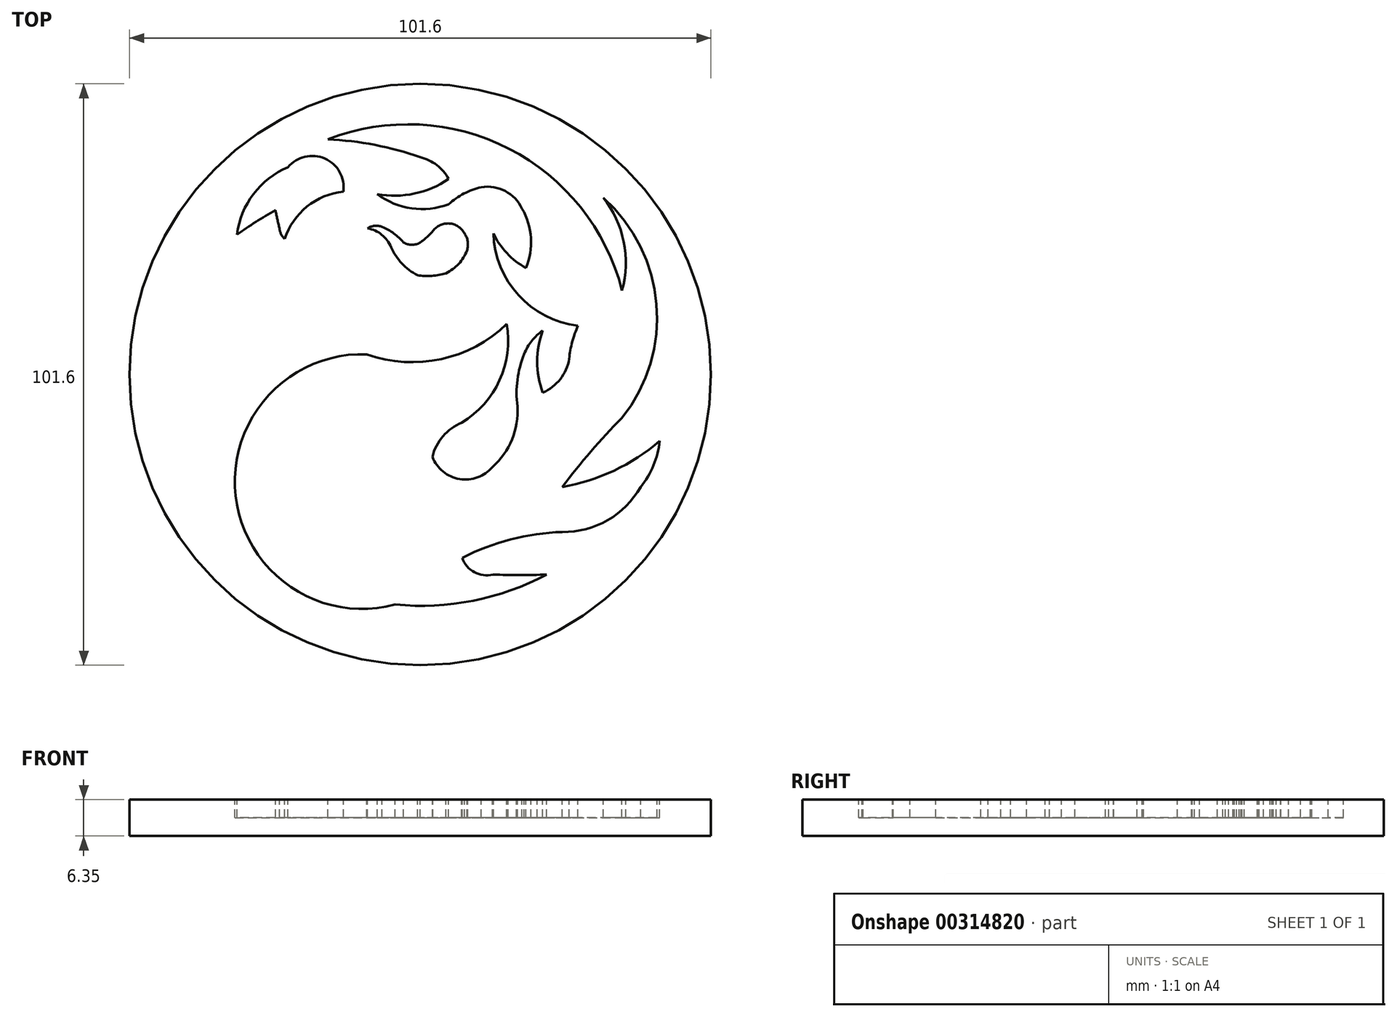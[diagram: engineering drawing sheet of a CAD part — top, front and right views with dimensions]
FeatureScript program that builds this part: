
annotation { "Feature Type Name" : "Feature", "Feature Type Description" : "" }
export const myFeature = defineFeature(function(context is Context, id is Id, definition is map)
    precondition{}
    {
        {
            var Q0;
            Q0=qCreatedBy(makeId("Top.planeOp"),FACE);
            var sketch = newSketch(context, id + "F0", { "sketchPlane" : qUnion([Q0])});
            skCircle(sketch, "E0", {"center": v(0, 0) * mm, "radius": 50.8 * mm});
            skSolve(sketch);
        }
        {
            var Q0;
            Q0 = qSketchRegion(id + "F0", true);
            extrude(context, id + "F1", {"entities" : qUnion([Q0]), "depth" : 6.35 * mm});
        }
        {
            var Q0;
            Q0=makeQuery(id+"F1.opExtrude","CAP_FACE",FACE,{"disambiguationData":[OSD([sQuery(id+"F0.wireOp",EDGE,"E0")])],"isStart":false});
            var sketch = newSketch(context, id + "F2", { "sketchPlane" : qUnion([Q0])});
            skArc(sketch, "E1", {"start": v(-9.32, 3.53) * mm, "mid": v(-32.25, -21.21) * mm, "end": v(-4.37, -40.2) * mm});
            skArc(sketch, "E2", {"start": v(-9.32, 3.53) * mm, "mid": v(3.65, 2.7) * mm, "end": v(15.11, 8.83) * mm});
            skArc(sketch, "E3", {"start": v(7.25, -8.43) * mm, "mid": v(13.85, -1.01) * mm, "end": v(15.11, 8.83) * mm});
            skArc(sketch, "E4", {"start": v(7.25, -8.43) * mm, "mid": v(3.96, -10.79) * mm, "end": v(2.13, -14.4) * mm});
            skArc(sketch, "E5", {"start": v(2.13, -14.4) * mm, "mid": v(6.88, -18.26) * mm, "end": v(12.62, -16.15) * mm});
            skArc(sketch, "E6", {"start": v(12.62, -16.15) * mm, "mid": v(16.03, -11.36) * mm, "end": v(16.97, -5.56) * mm});
            skArc(sketch, "E7", {"start": v(18.17, 3.59) * mm, "mid": v(16.98, -0.9) * mm, "end": v(16.97, -5.56) * mm});
            skArc(sketch, "E8", {"start": v(21.42, 7.69) * mm, "mid": v(19.5, 5.87) * mm, "end": v(18.17, 3.59) * mm});
            skArc(sketch, "E9", {"start": v(21.42, 7.69) * mm, "mid": v(20.44, 2.26) * mm, "end": v(21.42, -3.16) * mm});
            skArc(sketch, "E10", {"start": v(21.42, -3.16) * mm, "mid": v(24.47, -0.8) * mm, "end": v(26.03, 2.73) * mm});
            skArc(sketch, "E11", {"start": v(27.57, 8.54) * mm, "mid": v(26.56, 5.7) * mm, "end": v(26.03, 2.73) * mm});
            skArc(sketch, "E12", {"start": v(12.79, 24.69) * mm, "mid": v(17.16, 13.86) * mm, "end": v(27.57, 8.54) * mm});
            skArc(sketch, "E13", {"start": v(-4.37, -40.2) * mm, "mid": v(9.25, -39.51) * mm, "end": v(22.1, -34.94) * mm});
            skArc(sketch, "E14", {"start": v(12.7, -34.94) * mm, "mid": v(17.4, -35.05) * mm, "end": v(22.1, -34.94) * mm});
            skArc(sketch, "E15", {"start": v(7.32, -32.04) * mm, "mid": v(9.45, -34.52) * mm, "end": v(12.7, -34.94) * mm});
            skArc(sketch, "E16", {"start": v(24.83, -27.51) * mm, "mid": v(15.83, -28.81) * mm, "end": v(7.32, -32.04) * mm});
            skArc(sketch, "E17", {"start": v(24.83, -27.51) * mm, "mid": v(32.75, -25.46) * mm, "end": v(38.5, -19.65) * mm});
            skArc(sketch, "E18", {"start": v(38.5, -19.65) * mm, "mid": v(40.77, -15.89) * mm, "end": v(41.83, -11.62) * mm});
            skArc(sketch, "E19", {"start": v(24.83, -19.65) * mm, "mid": v(33.88, -16.79) * mm, "end": v(41.83, -11.62) * mm});
            skArc(sketch, "E20", {"start": v(35.25, -7.6) * mm, "mid": v(29.82, -13.43) * mm, "end": v(24.83, -19.65) * mm});
            skArc(sketch, "E21", {"start": v(35.25, -7.6) * mm, "mid": v(41.28, 12.3) * mm, "end": v(31.98, 30.9) * mm});
            skArc(sketch, "E22", {"start": v(35.25, 14.72) * mm, "mid": v(35.55, 23.2) * mm, "end": v(31.98, 30.9) * mm});
            skArc(sketch, "E23", {"start": v(35.25, 14.72) * mm, "mid": v(15.48, 39.47) * mm, "end": v(-16.16, 41.1) * mm});
            skArc(sketch, "E24", {"start": v(-7.5, 31.5) * mm, "mid": v(-1.01, 31.62) * mm, "end": v(4.96, 34.16) * mm});
            skArc(sketch, "E25", {"start": v(-7.5, 31.5) * mm, "mid": v(-1.5, 29.05) * mm, "end": v(4.96, 29.74) * mm});
            skArc(sketch, "E26", {"start": v(10.67, 32.73) * mm, "mid": v(7.62, 31.61) * mm, "end": v(4.96, 29.74) * mm});
            skArc(sketch, "E27", {"start": v(17.8, 29) * mm, "mid": v(14.86, 32.06) * mm, "end": v(10.67, 32.73) * mm});
            skArc(sketch, "E28", {"start": v(18.47, 18.62) * mm, "mid": v(19.35, 23.89) * mm, "end": v(17.8, 29) * mm});
            skArc(sketch, "E29", {"start": v(12.79, 24.69) * mm, "mid": v(15.14, 21.2) * mm, "end": v(18.47, 18.62) * mm});
            skArc(sketch, "E30", {"start": v(0, 37.98) * mm, "mid": v(-7.97, 40.13) * mm, "end": v(-16.16, 41.1) * mm});
            skArc(sketch, "E31", {"start": v(4.96, 34.16) * mm, "mid": v(2.89, 36.6) * mm, "end": v(0, 37.98) * mm});
            skArc(sketch, "E32", {"start": v(-13.44, 31.97) * mm, "mid": v(-16.67, 37.73) * mm, "end": v(-23.1, 36.23) * mm});
            skArc(sketch, "E33", {"start": v(-23.1, 36.23) * mm, "mid": v(-29.16, 31.54) * mm, "end": v(-32.01, 24.43) * mm});
            skArc(sketch, "E34", {"start": v(-25.31, 28.7) * mm, "mid": v(-28.74, 26.68) * mm, "end": v(-32.01, 24.43) * mm});
            skArc(sketch, "E35", {"start": v(-25.31, 28.7) * mm, "mid": v(-24.97, 27.11) * mm, "end": v(-24.6, 25.54) * mm});
            skArc(sketch, "E36", {"start": v(-24.6, 25.54) * mm, "mid": v(-24.32, 24.53) * mm, "end": v(-23.7, 23.68) * mm});
            skArc(sketch, "E37", {"start": v(-13.44, 31.97) * mm, "mid": v(-19.8, 29.35) * mm, "end": v(-23.7, 23.68) * mm});
            skArc(sketch, "E38", {"start": v(-5.09, 22.27) * mm, "mid": v(-6.72, 24.43) * mm, "end": v(-9.2, 25.54) * mm});
            skArc(sketch, "E39", {"start": v(-5.09, 22.27) * mm, "mid": v(-3.22, 19.4) * mm, "end": v(-0.49, 17.35) * mm});
            skArc(sketch, "E40", {"start": v(-0.49, 17.35) * mm, "mid": v(2.03, 17.24) * mm, "end": v(4.51, 17.7) * mm});
            skArc(sketch, "E41", {"start": v(4.51, 17.7) * mm, "mid": v(6.71, 19.34) * mm, "end": v(8.16, 21.69) * mm});
            skArc(sketch, "E42", {"start": v(8.16, 21.69) * mm, "mid": v(8.3, 23.24) * mm, "end": v(7.72, 24.69) * mm});
            skArc(sketch, "E43", {"start": v(7.72, 24.69) * mm, "mid": v(5.07, 26.4) * mm, "end": v(2.21, 25.07) * mm});
            skArc(sketch, "E44", {"start": v(0, 23.08) * mm, "mid": v(1.17, 24) * mm, "end": v(2.21, 25.07) * mm});
            skArc(sketch, "E45", {"start": v(-2.9, 23.08) * mm, "mid": v(-1.45, 22.68) * mm, "end": v(0, 23.08) * mm});
            skArc(sketch, "E46", {"start": v(-2.9, 23.08) * mm, "mid": v(-4.63, 24.66) * mm, "end": v(-6.66, 25.82) * mm});
            skArc(sketch, "E47", {"start": v(-6.66, 25.82) * mm, "mid": v(-7.96, 25.98) * mm, "end": v(-9.2, 25.54) * mm});
            skSolve(sketch);
        }
        {
            var Q0;
            Q0 = qSketchRegion(id + "F2", true);
            extrude(context, id + "F3", {"entities" : qUnion([Q0]), "operationType" : NewBodyOperationType.REMOVE, "oppositeDirection" : true, "depth" : 3.17 * mm});
        }
    });
